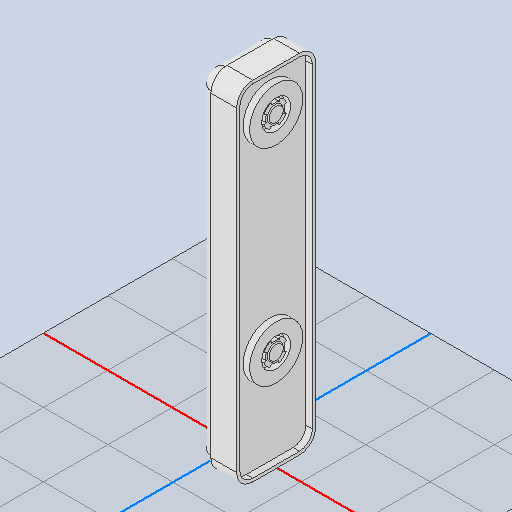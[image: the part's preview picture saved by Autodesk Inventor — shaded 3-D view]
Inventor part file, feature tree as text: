
AUTODESK INVENTOR PART (.ipt)
format: ipt  version: 2022 (Build 260153000, 153)  size: 888,832 bytes
history: native  units: mm
features: sketch x1, projected_geometry x1
ambient origin geometry x8: Origin, YZ Plane, XZ Plane, XY Plane, X Axis, Y Axis, Z Axis, Center Point
bodies: body (feature_tree), Solid1 (feature_tree)
feature tree (2):
  sketch  "Sketch1"
  projected_geometry  "Projected Loop1"
